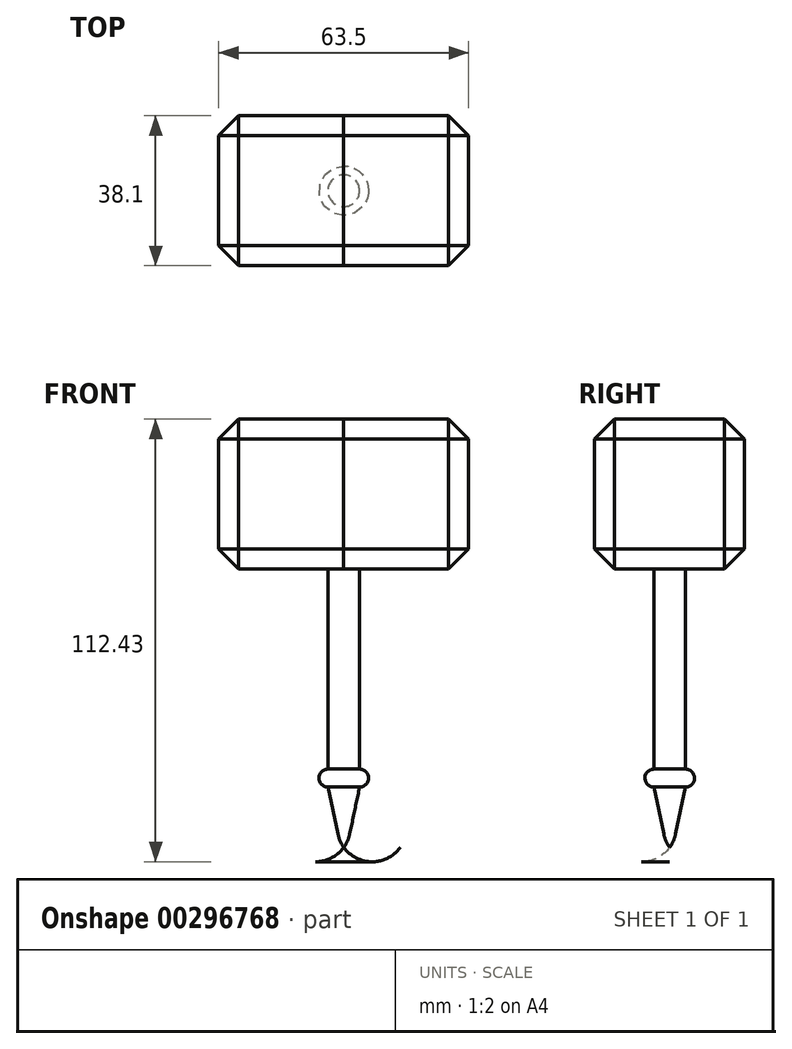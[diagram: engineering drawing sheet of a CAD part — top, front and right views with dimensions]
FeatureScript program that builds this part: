
annotation { "Feature Type Name" : "Feature", "Feature Type Description" : "" }
export const myFeature = defineFeature(function(context is Context, id is Id, definition is map)
    precondition{}
    {
        {
            var Q0;
            Q0=qCreatedBy(makeId("Front.planeOp"),FACE);
            var sketch = newSketch(context, id + "F0", { "sketchPlane" : qUnion([Q0])});
            skLineSegment(sketch, "E0.bottom", {"start": v(0, 0) * mm, "end": v(-4.02, 0) * mm});
            skLineSegment(sketch, "E0.top", {"start": v(0, -50.8) * mm, "end": v(-4.02, -50.8) * mm});
            skLineSegment(sketch, "E0.left", {"start": v(0, 0) * mm, "end": v(0, -50.8) * mm});
            skLineSegment(sketch, "E0.right", {"start": v(-4.02, 0) * mm, "end": v(-4.02, -50.8) * mm});
            skLineSegment(sketch, "E1", {"start": v(0, -50.8) * mm, "end": v(0, -59.94) * mm});
            skLineSegment(sketch, "E2", {"start": v(0, -55.37) * mm, "end": v(-4.02, -55.37) * mm});
            skPoint(sketch, "E2.endSnap0", {"position": v(0, -55.37) * mm});
            skLineSegment(sketch, "E3", {"start": v(-4.02, -55.37) * mm, "end": v(-1.5, -67.27) * mm});
            skLineSegment(sketch, "E4", {"start": v(0, -67.11) * mm, "end": v(0, -59.94) * mm});
            skArc(sketch, "E5", {"start": v(-4.02, -50.8) * mm, "mid": v(-6.3, -53.09) * mm, "end": v(-4.02, -55.37) * mm});
            skPoint(sketch, "E6.visualSharp", {"position": v(0, -74.42) * mm});
            skLineSegment(sketch, "E7", {"start": v(0, -67.11) * mm, "end": v(0, -70.67) * mm});
            skLineSegment(sketch, "E8", {"start": v(0, -70.67) * mm, "end": v(0, -74.42) * mm});
            skArc(sketch, "E9", {"start": v(-1.5, -67.27) * mm, "mid": v(-0.93, -69.05) * mm, "end": v(0, -70.67) * mm});
            skSolve(sketch);
        }
        {
            var Q0;
            Q0 = qSketchRegion(id + "F0", true);
            var Q1;
            Q1=sQuery(id+"F0.wireOp",EDGE,"E0.left");
            revolve(context, id + "F1", {"entities" : qUnion([Q0]), "axis" : qUnion([Q1]), "revolveType" : RevolveType.FULL});
        }
        {
            var Q0;
            Q0=qCreatedBy(makeId("Front.planeOp"),FACE);
            var sketch = newSketch(context, id + "F2", { "sketchPlane" : qUnion([Q0])});
            skLineSegment(sketch, "E10.bottom", {"start": v(-31.75, 0) * mm, "end": v(0, 0) * mm});
            skLineSegment(sketch, "E10.top", {"start": v(-31.75, 38.1) * mm, "end": v(0, 38.1) * mm});
            skLineSegment(sketch, "E10.left", {"start": v(-31.75, 0) * mm, "end": v(-31.75, 38.1) * mm});
            skLineSegment(sketch, "E10.right", {"start": v(0, 0) * mm, "end": v(0, 38.1) * mm});
            skSolve(sketch);
        }
        {
            var Q0;
            Q0=makeQuery(id+"F2.imprint","IMPRINT",FACE,{"disambiguationData":[TD([[makeQuery(id+"F2.imprint","IMPRINT",EDGE,{"derivedFrom":sQuery(id+"F2.wireOp",EDGE,"E10.bottom")}),1.0]])]});
            extrude(context, id + "F3", {"entities" : qUnion([Q0]), "endBound" : BoundingType.SYMMETRIC, "depth" : 38.1 * mm});
        }
        {
            var Q0;
            Q0=makeQuery(id+"F3.opExtrude","CAP_EDGE",EDGE,{"disambiguationData":[OSD([sQuery(id+"F2.wireOp",EDGE,"E10.top")])],"isStart":false});
            var Q1;
            Q1=makeQuery(id+"F3.opExtrude","SWEPT_EDGE",EDGE,{"disambiguationData":[OSD([sQuery(id+"F2.wireOp",EDGE,"E10.top"),sQuery(id+"F2.wireOp",EDGE,"E10.left")])]});
            var Q2;
            Q2=makeQuery(id+"F3.opExtrude","CAP_EDGE",EDGE,{"disambiguationData":[OSD([sQuery(id+"F2.wireOp",EDGE,"E10.top")])],"isStart":true});
            var Q3;
            Q3=makeQuery(id+"F3.opExtrude","CAP_EDGE",EDGE,{"disambiguationData":[OSD([sQuery(id+"F2.wireOp",EDGE,"E10.left")])],"isStart":false});
            var Q4;
            Q4=makeQuery(id+"F3.opExtrude","CAP_EDGE",EDGE,{"disambiguationData":[OSD([sQuery(id+"F2.wireOp",EDGE,"E10.bottom")])],"isStart":false});
            var Q5;
            Q5=makeQuery(id+"F3.opExtrude","SWEPT_FACE",FACE,{"disambiguationData":[OSD([sQuery(id+"F2.wireOp",EDGE,"E10.left")])]});
            var Q6;
            Q6=makeQuery(id+"F3.opExtrude","CAP_EDGE",EDGE,{"disambiguationData":[OSD([sQuery(id+"F2.wireOp",EDGE,"E10.bottom")])],"isStart":true});
            chamfer(context, id + "F4", {"entities" : qUnion([Q0, Q1, Q2, Q3, Q4, Q5, Q6]), "width" : 5.08 * mm, "tangentPropagation" : true});
        }
        {
            var Q0;
            Q0=makeQuery(id+"F3.opExtrude","SWEPT_BODY",BODY,{"disambiguationData":[OSD([sQuery(id+"F2.wireOp",EDGE,"E10.bottom"),sQuery(id+"F2.wireOp",EDGE,"E10.top"),sQuery(id+"F2.wireOp",EDGE,"E10.left"),sQuery(id+"F2.wireOp",EDGE,"E10.right")])]});
            var Q1;
            Q1=qCreatedBy(makeId("Right.planeOp"),FACE);
            mirror(context, id + "F5", {"entities" : qUnion([Q0]), "mirrorPlane" : qUnion([Q1])});
        }
    });
